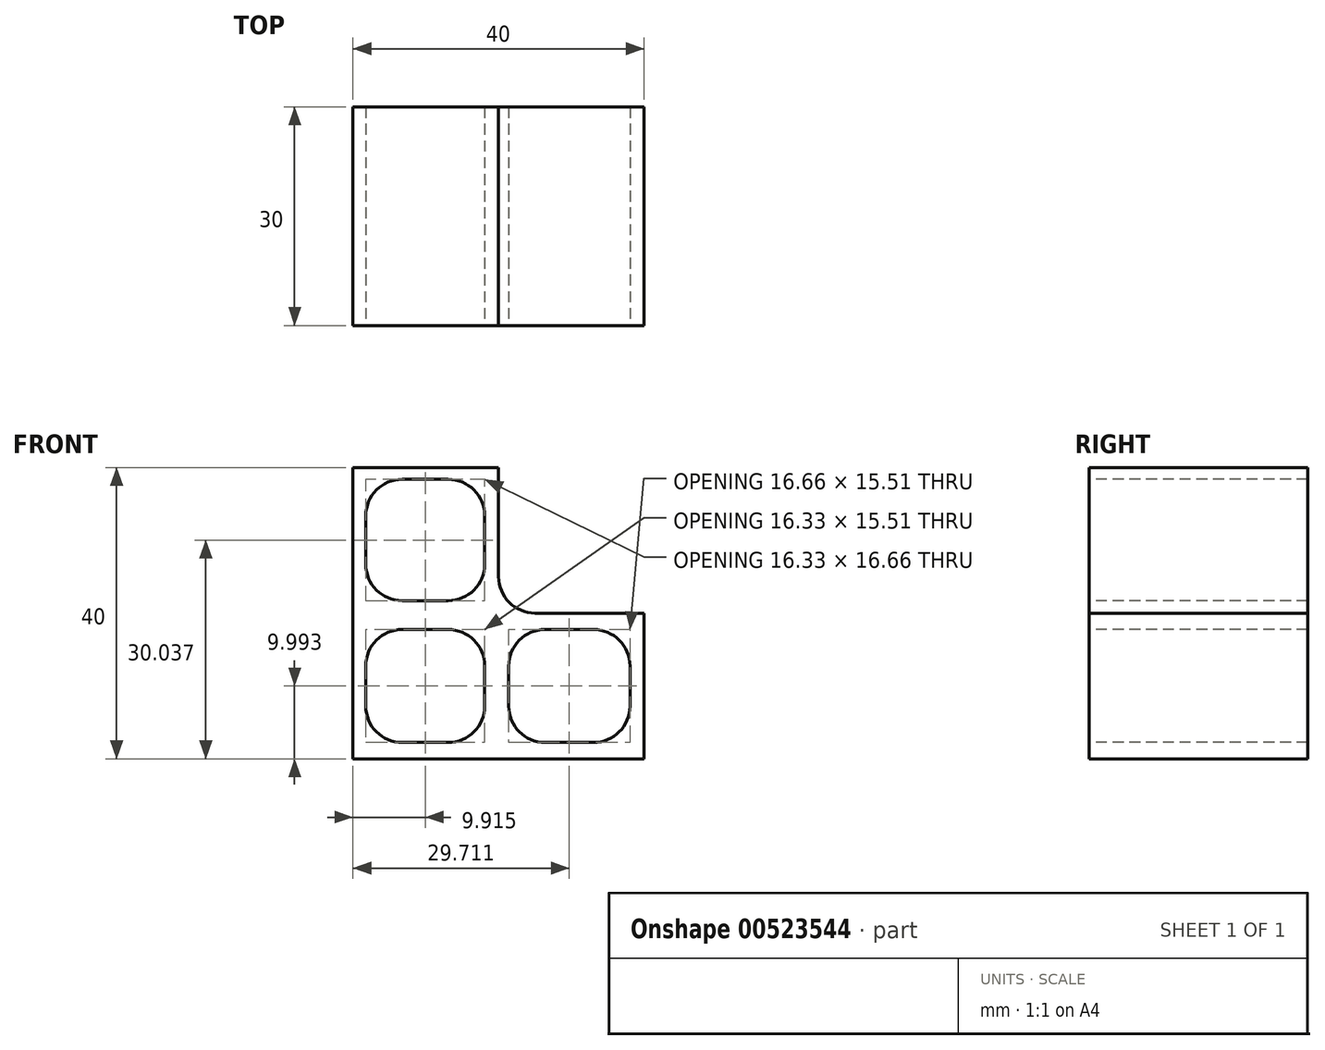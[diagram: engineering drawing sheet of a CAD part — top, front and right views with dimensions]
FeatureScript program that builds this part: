
annotation { "Feature Type Name" : "Feature", "Feature Type Description" : "" }
export const myFeature = defineFeature(function(context is Context, id is Id, definition is map)
    precondition{}
    {
        {
            var Q0;
            Q0=qCreatedBy(makeId("Front.planeOp"),FACE);
            var sketch = newSketch(context, id + "F0", { "sketchPlane" : qUnion([Q0])});
            skLineSegment(sketch, "E0.bottom", {"start": v(-20, 20) * mm, "end": v(20, 20) * mm});
            skLineSegment(sketch, "E0.top", {"start": v(-20, -20) * mm, "end": v(20, -20) * mm});
            skLineSegment(sketch, "E0.left", {"start": v(-20, 20) * mm, "end": v(-20, -20) * mm});
            skLineSegment(sketch, "E0.right", {"start": v(20, 20) * mm, "end": v(20, -20) * mm});
            skPoint(sketch, "E0.middle", {"position": v(0, 0) * mm});
            skSolve(sketch);
        }
        {
            var Q0;
            Q0=makeQuery(id+"F0.imprint","IMPRINT",FACE,{"disambiguationData":[TD([[makeQuery(id+"F0.imprint","IMPRINT",EDGE,{"derivedFrom":sQuery(id+"F0.wireOp",EDGE,"E0.bottom")}),-1.0]])]});
            extrude(context, id + "F1", {"entities" : qUnion([Q0]), "depth" : 30 * mm, "offsetDistance" : 25 * mm});
        }
        {
            var Q0;
            Q0=makeQuery(id+"F1.opExtrude","CAP_FACE",FACE,{"disambiguationData":[OSD([sQuery(id+"F0.wireOp",EDGE,"E0.bottom"),sQuery(id+"F0.wireOp",EDGE,"E0.top"),sQuery(id+"F0.wireOp",EDGE,"E0.left"),sQuery(id+"F0.wireOp",EDGE,"E0.right")])],"isStart":false});
            var sketch = newSketch(context, id + "F2", { "sketchPlane" : qUnion([Q0])});
            skLineSegment(sketch, "E1.bottom", {"start": v(23.16, 23.98) * mm, "end": v(0, 23.98) * mm});
            skLineSegment(sketch, "E1.top", {"start": v(23.16, 0) * mm, "end": v(0, 0) * mm});
            skLineSegment(sketch, "E1.left", {"start": v(23.16, 23.98) * mm, "end": v(23.16, 0) * mm});
            skLineSegment(sketch, "E1.right", {"start": v(0, 23.98) * mm, "end": v(0, 0) * mm});
            skLineSegment(sketch, "E2.bottom", {"start": v(-18.25, 18.37) * mm, "end": v(-1.92, 18.37) * mm});
            skLineSegment(sketch, "E2.top", {"start": v(-18.25, 1.7) * mm, "end": v(-1.92, 1.7) * mm});
            skLineSegment(sketch, "E2.left", {"start": v(-18.25, 18.37) * mm, "end": v(-18.25, 1.7) * mm});
            skLineSegment(sketch, "E2.right", {"start": v(-1.92, 18.37) * mm, "end": v(-1.92, 1.7) * mm});
            skLineSegment(sketch, "E3.bottom", {"start": v(-18.25, -17.76) * mm, "end": v(-1.92, -17.76) * mm});
            skLineSegment(sketch, "E3.top", {"start": v(-18.25, -2.25) * mm, "end": v(-1.92, -2.25) * mm});
            skLineSegment(sketch, "E3.left", {"start": v(-18.25, -17.76) * mm, "end": v(-18.25, -2.25) * mm});
            skLineSegment(sketch, "E3.right", {"start": v(-1.92, -17.76) * mm, "end": v(-1.92, -2.25) * mm});
            skLineSegment(sketch, "E4.bottom", {"start": v(18.04, -2.25) * mm, "end": v(1.38, -2.25) * mm});
            skLineSegment(sketch, "E4.top", {"start": v(18.04, -17.76) * mm, "end": v(1.38, -17.76) * mm});
            skLineSegment(sketch, "E4.left", {"start": v(18.04, -2.25) * mm, "end": v(18.04, -17.76) * mm});
            skLineSegment(sketch, "E4.right", {"start": v(1.38, -2.25) * mm, "end": v(1.38, -17.76) * mm});
            skSolve(sketch);
        }
        {
            var Q0;
            {var subQ0=sQuery(id+"F2.wireOp",EDGE,"E1.right");var subQ1=sQuery(id+"F2.wireOp",EDGE,"E1.top");var subQ2=makeQuery(id+"F2.imprint","INTERSECT",VERTEX,{"derivedFrom":[subQ1,subQ0]});Q0=makeQuery(id+"F2.imprint","IMPRINT",FACE,{"disambiguationData":[TD([[makeQuery(id+"F2.imprint","IMPRINT",EDGE,{"disambiguationData":[TD([[subQ2,1.0]])],"derivedFrom":subQ1}),-1.0]])]});}
            var Q1;
            Q1=makeQuery(id+"F2.imprint","IMPRINT",FACE,{"disambiguationData":[TD([[makeQuery(id+"F2.imprint","IMPRINT",EDGE,{"derivedFrom":sQuery(id+"F2.wireOp",EDGE,"E2.bottom")}),-1.0]])]});
            var Q2;
            Q2=makeQuery(id+"F2.imprint","IMPRINT",FACE,{"disambiguationData":[TD([[makeQuery(id+"F2.imprint","IMPRINT",EDGE,{"derivedFrom":sQuery(id+"F2.wireOp",EDGE,"E3.bottom")}),1.0]])]});
            var Q3;
            Q3=makeQuery(id+"F2.imprint","IMPRINT",FACE,{"disambiguationData":[TD([[makeQuery(id+"F2.imprint","IMPRINT",EDGE,{"derivedFrom":sQuery(id+"F2.wireOp",EDGE,"E4.bottom")}),1.0]])]});
            extrude(context, id + "F3", {"entities" : qUnion([Q0, Q1, Q2, Q3]), "operationType" : NewBodyOperationType.REMOVE, "endBound" : BoundingType.UP_TO_NEXT, "oppositeDirection" : true, "depth" : 25 * mm, "offsetDistance" : 25 * mm});
        }
        {
            var Q0;
            Q0=makeQuery(id+"F3.boolean.opBoolean","COPY",EDGE,{"derivedFrom":makeQuery(id+"F3.opExtrude","SWEPT_EDGE",EDGE,{"disambiguationData":[OSD([sQuery(id+"F2.wireOp",EDGE,"E1.top"),sQuery(id+"F2.wireOp",EDGE,"E1.right")])]})});
            var Q1;
            Q1=makeQuery(id+"F3.boolean.opBoolean","COPY",EDGE,{"derivedFrom":makeQuery(id+"F3.opExtrude","SWEPT_EDGE",EDGE,{"disambiguationData":[OSD([sQuery(id+"F2.wireOp",EDGE,"E2.bottom"),sQuery(id+"F2.wireOp",EDGE,"E2.left")])]})});
            var Q2;
            Q2=makeQuery(id+"F3.boolean.opBoolean","COPY",EDGE,{"derivedFrom":makeQuery(id+"F3.opExtrude","SWEPT_EDGE",EDGE,{"disambiguationData":[OSD([sQuery(id+"F2.wireOp",EDGE,"E2.bottom"),sQuery(id+"F2.wireOp",EDGE,"E2.right")])]})});
            var Q3;
            Q3=makeQuery(id+"F3.boolean.opBoolean","COPY",EDGE,{"derivedFrom":makeQuery(id+"F3.opExtrude","SWEPT_EDGE",EDGE,{"disambiguationData":[OSD([sQuery(id+"F2.wireOp",EDGE,"E2.top"),sQuery(id+"F2.wireOp",EDGE,"E2.left")])]})});
            var Q4;
            Q4=makeQuery(id+"F3.boolean.opBoolean","COPY",EDGE,{"derivedFrom":makeQuery(id+"F3.opExtrude","SWEPT_EDGE",EDGE,{"disambiguationData":[OSD([sQuery(id+"F2.wireOp",EDGE,"E2.top"),sQuery(id+"F2.wireOp",EDGE,"E2.right")])]})});
            var Q5;
            Q5=makeQuery(id+"F3.boolean.opBoolean","COPY",EDGE,{"derivedFrom":makeQuery(id+"F3.opExtrude","SWEPT_EDGE",EDGE,{"disambiguationData":[OSD([sQuery(id+"F2.wireOp",EDGE,"E3.bottom"),sQuery(id+"F2.wireOp",EDGE,"E3.right")])]})});
            var Q6;
            Q6=makeQuery(id+"F3.boolean.opBoolean","COPY",EDGE,{"derivedFrom":makeQuery(id+"F3.opExtrude","SWEPT_EDGE",EDGE,{"disambiguationData":[OSD([sQuery(id+"F2.wireOp",EDGE,"E4.top"),sQuery(id+"F2.wireOp",EDGE,"E4.left")])]})});
            var Q7;
            Q7=makeQuery(id+"F3.boolean.opBoolean","COPY",EDGE,{"derivedFrom":makeQuery(id+"F3.opExtrude","SWEPT_EDGE",EDGE,{"disambiguationData":[OSD([sQuery(id+"F2.wireOp",EDGE,"E4.bottom"),sQuery(id+"F2.wireOp",EDGE,"E4.left")])]})});
            var Q8;
            Q8=makeQuery(id+"F3.boolean.opBoolean","COPY",EDGE,{"derivedFrom":makeQuery(id+"F3.opExtrude","SWEPT_EDGE",EDGE,{"disambiguationData":[OSD([sQuery(id+"F2.wireOp",EDGE,"E3.top"),sQuery(id+"F2.wireOp",EDGE,"E3.right")])]})});
            var Q9;
            Q9=makeQuery(id+"F3.boolean.opBoolean","COPY",EDGE,{"derivedFrom":makeQuery(id+"F3.opExtrude","SWEPT_EDGE",EDGE,{"disambiguationData":[OSD([sQuery(id+"F2.wireOp",EDGE,"E3.top"),sQuery(id+"F2.wireOp",EDGE,"E3.left")])]})});
            var Q10;
            Q10=makeQuery(id+"F3.boolean.opBoolean","COPY",EDGE,{"derivedFrom":makeQuery(id+"F3.opExtrude","SWEPT_EDGE",EDGE,{"disambiguationData":[OSD([sQuery(id+"F2.wireOp",EDGE,"E4.bottom"),sQuery(id+"F2.wireOp",EDGE,"E4.right")])]})});
            var Q11;
            Q11=makeQuery(id+"F3.boolean.opBoolean","COPY",EDGE,{"derivedFrom":makeQuery(id+"F3.opExtrude","SWEPT_EDGE",EDGE,{"disambiguationData":[OSD([sQuery(id+"F2.wireOp",EDGE,"E3.bottom"),sQuery(id+"F2.wireOp",EDGE,"E3.left")])]})});
            var Q12;
            Q12=makeQuery(id+"F3.boolean.opBoolean","COPY",EDGE,{"derivedFrom":makeQuery(id+"F3.opExtrude","SWEPT_EDGE",EDGE,{"disambiguationData":[OSD([sQuery(id+"F2.wireOp",EDGE,"E4.top"),sQuery(id+"F2.wireOp",EDGE,"E4.right")])]})});
            fillet(context, id + "F4", {"entities" : qUnion([Q0, Q1, Q2, Q3, Q4, Q5, Q6, Q7, Q8, Q9, Q10, Q11, Q12]), "radius" : 5 * mm, "tangentPropagation" : true, "allowEdgeOverflow" : false});
        }
    });
